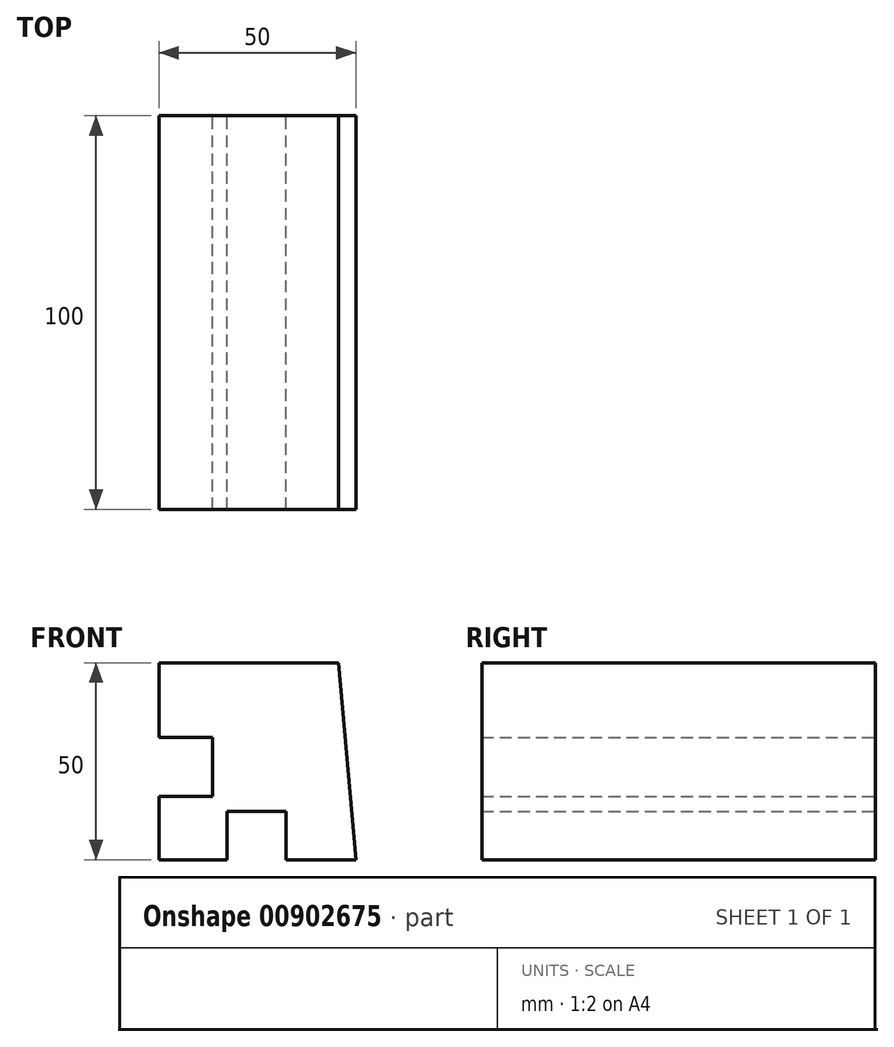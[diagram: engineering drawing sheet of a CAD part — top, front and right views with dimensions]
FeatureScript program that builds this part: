
annotation { "Feature Type Name" : "Feature", "Feature Type Description" : "" }
export const myFeature = defineFeature(function(context is Context, id is Id, definition is map)
    precondition{}
    {
        {
            var Q0;
            Q0=qCreatedBy(makeId("Front.planeOp"),FACE);
            var sketch = newSketch(context, id + "F0", { "sketchPlane" : qUnion([Q0])});
            skLineSegment(sketch, "E0.bottom", {"start": v(-23.73, 18.93) * mm, "end": v(21.9, 18.93) * mm});
            skLineSegment(sketch, "E0.top", {"start": v(-23.73, -31.07) * mm, "end": v(-6.44, -31.07) * mm});
            skLineSegment(sketch, "E0.left", {"start": v(-23.73, 18.93) * mm, "end": v(-23.73, 0) * mm});
            skLineSegment(sketch, "E1", {"start": v(21.9, 18.93) * mm, "end": v(26.27, -31.07) * mm});
            skLineSegment(sketch, "E2.bottom", {"start": v(-23.73, 0) * mm, "end": v(-10.07, 0) * mm});
            skLineSegment(sketch, "E2.top", {"start": v(-23.73, -15) * mm, "end": v(-10.07, -15) * mm});
            skLineSegment(sketch, "E2.right", {"start": v(-10.07, 0) * mm, "end": v(-10.07, -15) * mm});
            skLineSegment(sketch, "E3.trimOffspring", {"start": v(-23.73, -15) * mm, "end": v(-23.73, -31.07) * mm});
            skLineSegment(sketch, "E4", {"start": v(-6.44, -31.07) * mm, "end": v(-6.44, -18.81) * mm});
            skLineSegment(sketch, "E5", {"start": v(-6.44, -18.81) * mm, "end": v(8.5, -18.81) * mm});
            skLineSegment(sketch, "E6", {"start": v(8.5, -18.81) * mm, "end": v(8.5, -31.07) * mm});
            skLineSegment(sketch, "E7.trimOffspring", {"start": v(8.5, -31.07) * mm, "end": v(26.27, -31.07) * mm});
            skSolve(sketch);
        }
        {
            var Q0;
            Q0=makeQuery(id+"F0.imprint","IMPRINT",FACE,{"disambiguationData":[TD([[makeQuery(id+"F0.imprint","IMPRINT",EDGE,{"derivedFrom":sQuery(id+"F0.wireOp",EDGE,"E0.bottom")}),-1.0]])]});
            extrude(context, id + "F1", {"entities" : qUnion([Q0]), "depth" : 100 * mm, "offsetDistance" : 25 * mm});
        }
    });
